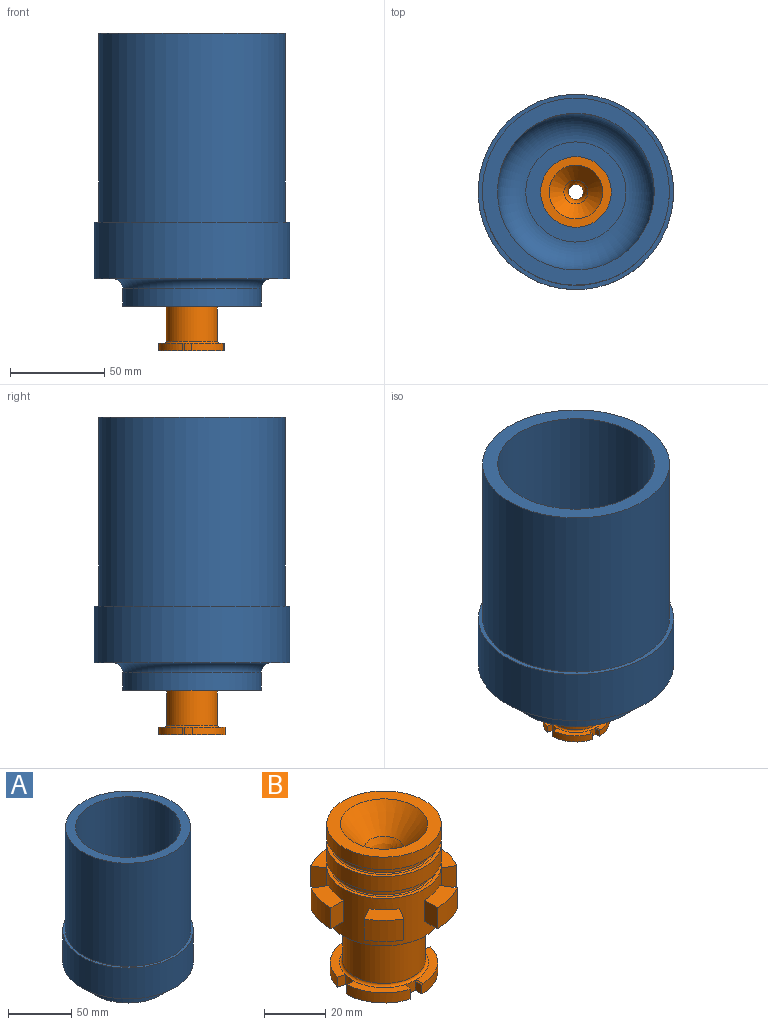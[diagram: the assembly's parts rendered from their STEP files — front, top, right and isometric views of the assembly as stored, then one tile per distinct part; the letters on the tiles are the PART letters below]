
ASSEMBLY  parts=2 mates=1
PART A: 38 faces, bbox 103.5x103.5x144.5 mm
  f0: plane 73.5x73.5mm, normal (0,0,-1), area 2735.3mm2, adj f1,f3,f5,f7,f10,f12,f24,f25
  f1: cylinder r=18.7mm len=6.84mm, axis (0,0,1), area 58.7mm2, adj f0,f11,f26,f37
  f2: plane 12.35x8.51mm, normal (0,0,1), area 68.2mm2, adj f3,f12,f35,f36
  f3: cylinder r=18.7mm len=9.35mm, axis (0,0,1), area 58.7mm2, adj f0,f2,f35,f36
  f4: plane 12.35x8.51mm, normal (0,0,1), area 68.2mm2, adj f5,f12,f33,f34
  f5: cylinder r=18.7mm len=9.35mm, axis (0,0,1), area 58.7mm2, adj f0,f4,f33,f34
  f6: plane 12.04x12.04mm, normal (0,0,1), area 68.2mm2, adj f7,f12,f31,f32
  f7: cylinder r=18.7mm len=6.84mm, axis (0,0,1), area 58.7mm2, adj f0,f6,f31,f32
  f8: plane 12.35x8.51mm, normal (0,0,1), area 68.2mm2, adj f10,f12,f29,f30
  f9: plane 12.35x8.51mm, normal (0,0,1), area 68.2mm2, adj f12,f25,f27,f28
  f10: cylinder r=18.7mm len=9.35mm, axis (0,0,1), area 58.7mm2, adj f0,f8,f29,f30
  f11: plane 12.04x12.04mm, normal (0,0,1), area 68.2mm2, adj f1,f12,f26,f37
  f12: cylinder r=24.7mm len=49.4mm, axis (0,0,1), area 1784.7mm2, adj f0,f2,f4,f6,f8,f9,f11,f13
  f13: plane 49.4x49.4mm, normal (0,0,-1), area 818.1mm2, adj f12,f14
  f14: cylinder r=18.7mm len=37.4mm, axis (0,0,1), area 2467.4mm2, adj f13,f15
  f15: plane 53.06x53.06mm, normal (0,0,1), area 1112.6mm2, adj f14,f16
  f16: torus R=26.53mm, axis (0,0,1), area 5341.3mm2, adj f15,f17
  f17: cylinder r=41.53mm len=94mm, axis (0,0,1), area 24528.4mm2, adj f16,f18
  f18: plane 99.06x99.06mm, normal (0,0,1), area 2288.6mm2, adj f17,f19
  f19: cylinder r=49.53mm len=100mm, axis (0,0,1), area 31120.6mm2, adj f18,f20
  f20: plane 103.5x103.5mm, normal (0,0,1), area 706.4mm2, adj f19,f21
  f21: cylinder r=51.75mm len=103.5mm, axis (0,0,1), area 9754.6mm2, adj f20,f22
  f22: plane 103.5x103.5mm, normal (0,0,-1), area 2937.4mm2, adj f21,f23
  f23: torus R=41.75mm, axis (0,0,1), area 1903.2mm2, adj f22,f24
  f24: cylinder r=36.75mm len=73.5mm, axis (0,0,1), area 2193.6mm2, adj f0,f23
  f25: cylinder r=18.7mm len=9.35mm, axis (0,0,1), area 58.7mm2, adj f0,f9,f27,f28
  f26: plane 6x5.2mm, normal (0.87,-0.5,0), area 36mm2, adj f0,f1,f11,f12
  f27: plane 6x6mm, normal (-1,0,0), area 36mm2, adj f0,f9,f12,f25
  f28: plane 6x5.2mm, normal (0.87,0.5,0), area 36mm2, adj f0,f9,f12,f25
  f29: plane 6x5.2mm, normal (-0.5,-0.87,0), area 36mm2, adj f0,f8,f10,f12
  f30: plane 6x6mm, normal (0,1,0), area 36mm2, adj f0,f8,f10,f12
  f31: plane 6x5.2mm, normal (0.5,-0.87,0), area 36mm2, adj f0,f6,f7,f12
  f32: plane 6x5.2mm, normal (-0.87,0.5,0), area 36mm2, adj f0,f6,f7,f12
  f33: plane 6x6mm, normal (1,0,0), area 36mm2, adj f0,f4,f5,f12
  f34: plane 6x5.2mm, normal (-0.87,-0.5,0), area 36mm2, adj f0,f4,f5,f12
  f35: plane 6x5.2mm, normal (0.5,0.87,0), area 36mm2, adj f0,f2,f3,f12
  f36: plane 6x6mm, normal (0,-1,0), area 36mm2, adj f0,f2,f3,f12
  f37: plane 6x5.2mm, normal (-0.5,0.87,0), area 36mm2, adj f0,f1,f11,f12
PART B: 77 faces, bbox 49.3x49.3x59.1 mm
  f0: plane 16.33x13.53mm, normal (0,0,1), area 60.6mm2, adj f41,f43,f61,f73
  f1: cylinder r=17.5mm len=16.83mm, axis (0,0,1), area 90.5mm2, adj f2,f44,f68,f70,f74
  f2: plane 16.33x13.53mm, normal (0,0,1), area 60.6mm2, adj f1,f41,f70,f74
  f3: cylinder r=17.5mm len=16.83mm, axis (0,0,1), area 90.5mm2, adj f4,f44,f65,f67,f75
  f4: plane 16.33x13.53mm, normal (0,0,1), area 60.6mm2, adj f3,f41,f67,f75
  f5: cylinder r=17.5mm len=16.83mm, axis (0,0,1), area 90.5mm2, adj f42,f44,f62,f64,f76
  f6: cylinder r=24.65mm len=9.14mm, axis (0,0,1), area 109.5mm2, adj f7,f8,f50,f60
  f7: plane 12.08x12.06mm, normal (0,0,1), area 68.2mm2, adj f6,f38,f50,f60
  f8: plane 12.08x12.06mm, normal (0,0,-1), area 68.2mm2, adj f6,f38,f50,f60
  f9: cylinder r=24.65mm len=12.46mm, axis (0,0,1), area 109.5mm2, adj f10,f11,f58,f59
  f10: plane 12.46x8.46mm, normal (0,0,1), area 68.2mm2, adj f9,f38,f58,f59
  f11: plane 12.46x8.46mm, normal (0,0,-1), area 68.2mm2, adj f9,f38,f58,f59
  f12: cylinder r=24.65mm len=12.44mm, axis (0,0,1), area 109.5mm2, adj f13,f14,f55,f57
  f13: plane 12.44x8.51mm, normal (0,0,1), area 68.2mm2, adj f12,f38,f55,f57
  f14: plane 12.44x8.51mm, normal (0,0,-1), area 68.2mm2, adj f12,f38,f55,f57
  f15: cylinder r=24.65mm len=9.14mm, axis (0,0,1), area 109.5mm2, adj f16,f17,f54,f56
  f16: plane 12.08x12.06mm, normal (0,0,1), area 68.2mm2, adj f15,f38,f54,f56
  f17: plane 12.08x12.06mm, normal (0,0,-1), area 68.2mm2, adj f15,f38,f54,f56
  f18: cylinder r=24.65mm len=12.46mm, axis (0,0,1), area 109.5mm2, adj f19,f20,f52,f53
  f19: plane 12.46x8.46mm, normal (0,0,1), area 68.2mm2, adj f18,f38,f52,f53
  f20: plane 12.46x8.46mm, normal (0,0,-1), area 68.2mm2, adj f18,f38,f52,f53
  f21: cone r=14.22mm half-angle=40deg, axis (0,0,1), area 791.5mm2, adj f22,f48
  f22: plane 37.4x37.4mm, normal (0,0,1), area 463.6mm2, adj f21,f23
  f23: cylinder r=18.7mm len=37.4mm, axis (0,0,1), area 587.5mm2, adj f22,f24
  f24: plane 37.4x37.4mm, normal (0,0,-1), area 145.2mm2, adj f23,f25
  f25: torus R=17.42mm, axis (0,0,1), area 67.8mm2, adj f24,f26
  f26: cylinder r=17.02mm len=34.04mm, axis (0,0,1), area 213.9mm2, adj f25,f27
  f27: torus R=17.42mm, axis (0,0,1), area 67.8mm2, adj f26,f28
  f28: plane 37.4x37.4mm, normal (0,0,1), area 145.2mm2, adj f27,f29
  f29: cylinder r=18.7mm len=37.4mm, axis (0,0,1), area 705mm2, adj f28,f30
  f30: plane 37.4x37.4mm, normal (0,0,-1), area 145.2mm2, adj f29,f31
  f31: torus R=17.42mm, axis (0,0,1), area 67.8mm2, adj f30,f32
  f32: cylinder r=17.02mm len=34.04mm, axis (0,0,1), area 213.9mm2, adj f31,f33
  f33: torus R=17.42mm, axis (0,0,1), area 67.8mm2, adj f32,f34
  f34: plane 37.4x37.4mm, normal (0,0,1), area 145.2mm2, adj f33,f38
  f35: plane 12.44x8.51mm, normal (0,0,1), area 68.2mm2, adj f36,f38,f49,f51
  f36: cylinder r=24.65mm len=12.44mm, axis (0,0,1), area 109.5mm2, adj f35,f37,f49,f51
  f37: plane 12.44x8.51mm, normal (0,0,-1), area 68.2mm2, adj f36,f38,f49,f51
  f38: cylinder r=18.7mm len=37.4mm, axis (0,0,1), area 1722.1mm2, adj f7,f8,f10,f11,f13,f14,f16,f17
  f39: plane 37.4x37.4mm, normal (0,0,-1), area 526mm2, adj f38,f40
  f40: cylinder r=13.5mm len=27mm, axis (0,0,1), area 1581.1mm2, adj f39,f41
  f41: torus R=14.5mm, axis (0,0,1), area 136.8mm2, adj f0,f2,f4,f40,f42,f63,f66,f69
  f42: plane 16.33x13.53mm, normal (0,0,1), area 60.6mm2, adj f5,f41,f64,f76
  f43: cylinder r=17.5mm len=16.83mm, axis (0,0,1), area 90.5mm2, adj f0,f44,f61,f71,f73
  f44: plane 35x35mm, normal (0,0,-1), area 625.4mm2, adj f1,f3,f5,f43,f45,f61,f62,f63
  f45: cone r=4.15mm half-angle=10deg, axis (0,0,-1), area 1320.9mm2, adj f44,f46
  f46: torus R=14mm, axis (0,0,1), area 44.4mm2, adj f45,f47
  f47: cylinder r=4mm len=11.26mm, axis (0,0,1), area 282.9mm2, adj f46,f48
  f48: torus R=14mm, axis (0,0,1), area 210.2mm2, adj f21,f47
  f49: plane 8.4x5.95mm, normal (1,0,0), area 50mm2, adj f35,f36,f37,f38
  f50: plane 8.4x5.17mm, normal (-0.87,0.5,0), area 50mm2, adj f6,f7,f8,f38
  f51: plane 8.4x5.14mm, normal (-0.86,-0.5,0), area 50mm2, adj f35,f36,f37,f38
  f52: plane 8.4x5.15mm, normal (0.5,0.87,0), area 50mm2, adj f18,f19,f20,f38
  f53: plane 8.4x5.95mm, normal (0.01,-1,0), area 50mm2, adj f18,f19,f20,f38
  f54: plane 8.4x5.15mm, normal (-0.5,0.87,0), area 50mm2, adj f15,f16,f17,f38
  f55: plane 8.4x5.95mm, normal (-1,0,0), area 50mm2, adj f12,f13,f14,f38
  f56: plane 8.4x5.17mm, normal (0.87,-0.5,0), area 50mm2, adj f15,f16,f17,f38
  f57: plane 8.4x5.14mm, normal (0.86,0.5,0), area 50mm2, adj f12,f13,f14,f38
  f58: plane 8.4x5.15mm, normal (-0.5,-0.87,0), area 50mm2, adj f9,f10,f11,f38
  f59: plane 8.4x5.95mm, normal (-0.01,1,0), area 50mm2, adj f9,f10,f11,f38
  f60: plane 8.4x5.15mm, normal (0.5,-0.87,0), area 50mm2, adj f6,f7,f8,f38
  f61: plane 4x2.89mm, normal (0.96,-0.27,0), area 12mm2, adj f0,f43,f44,f63
  f62: plane 3.5x3mm, normal (-1,0,0), area 10.5mm2, adj f5,f44,f63,f76
  f63: cylinder r=14.5mm len=4.46mm, axis (0,0,-1), area 16.2mm2, adj f41,f44,f61,f62,f76
  f64: plane 4x2.89mm, normal (0.27,0.96,0), area 12mm2, adj f5,f42,f44,f66
  f65: plane 3.5x3mm, normal (0,-1,0), area 10.5mm2, adj f3,f44,f66,f75
  f66: cylinder r=14.5mm len=4.46mm, axis (0,0,-1), area 16.2mm2, adj f41,f44,f64,f65,f75
  f67: plane 4x2.89mm, normal (-0.96,0.27,0), area 12mm2, adj f3,f4,f44,f69
  f68: plane 3.5x3mm, normal (1,0,0), area 10.5mm2, adj f1,f44,f69,f74
  f69: cylinder r=14.5mm len=4.46mm, axis (0,0,-1), area 16.2mm2, adj f41,f44,f67,f68,f74
  f70: plane 4x2.89mm, normal (-0.27,-0.96,0), area 12mm2, adj f1,f2,f44,f72
  f71: plane 3.5x3mm, normal (0,1,0), area 10.5mm2, adj f43,f44,f72,f73
  f72: cylinder r=14.5mm len=4.46mm, axis (0,0,-1), area 16.2mm2, adj f41,f44,f70,f71,f73
  f73: plane 3.01x0.5mm, normal (0,0.71,0.71), area 2.1mm2, adj f0,f43,f71,f72
  f74: plane 3.01x0.5mm, normal (0.71,0,0.71), area 2.1mm2, adj f1,f2,f68,f69
  f75: plane 3.01x0.5mm, normal (0,-0.71,0.71), area 2.1mm2, adj f3,f4,f65,f66
  f76: plane 3.01x0.5mm, normal (-0.71,0,0.71), area 2.1mm2, adj f5,f42,f62,f63
PLACE A t=(-6.47,22.2,-18.85)mm fixed
PLACE B t=(-6.47,22.2,-33.25)mm
MATE cylindrical A.f1 <-> B.f1  axis (0,0,-1) through (-6.47,22.2,-33.35)mm
